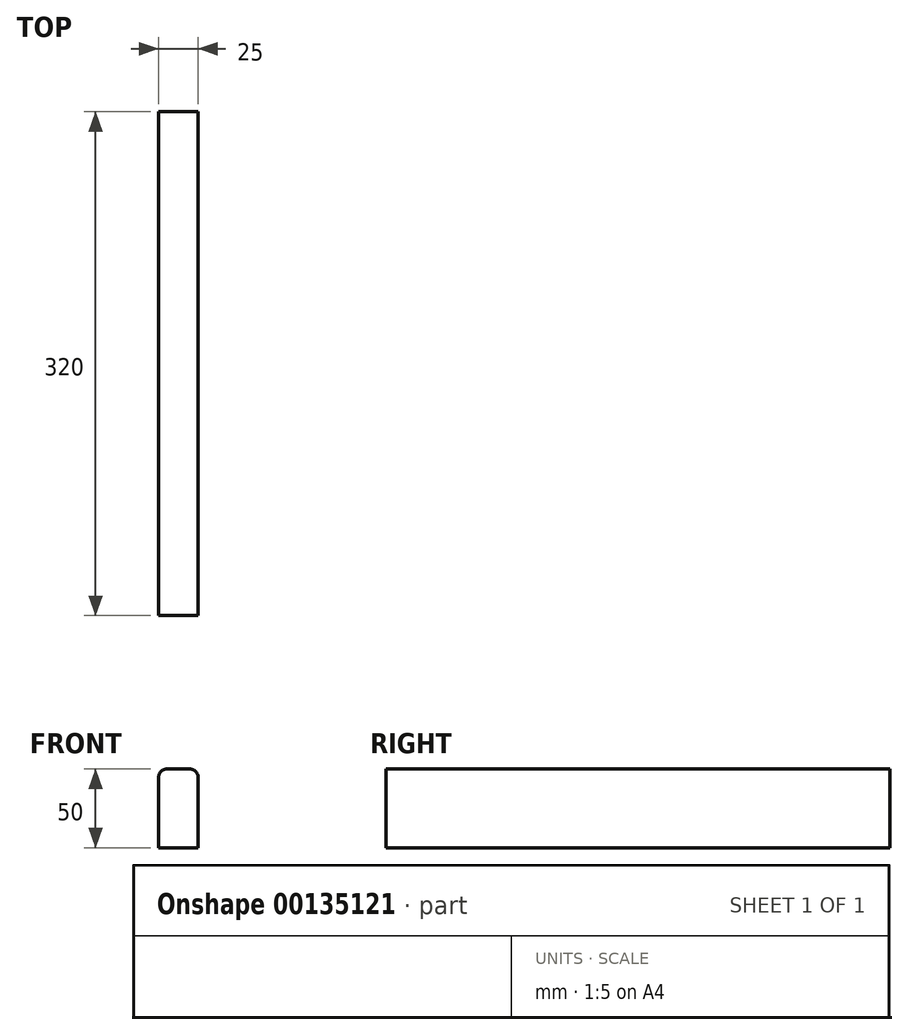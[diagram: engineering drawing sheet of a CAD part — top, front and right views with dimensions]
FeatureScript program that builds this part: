
annotation { "Feature Type Name" : "Feature", "Feature Type Description" : "" }
export const myFeature = defineFeature(function(context is Context, id is Id, definition is map)
    precondition{}
    {
        {
            var Q0;
            Q0=qCreatedBy(makeId("Front.planeOp"),FACE);
            var sketch = newSketch(context, id + "F0", { "sketchPlane" : qUnion([Q0])});
            skLineSegment(sketch, "E0.bottom", {"start": v(0, 0) * mm, "end": v(25, 0) * mm});
            skLineSegment(sketch, "E0.top", {"start": v(5, 50) * mm, "end": v(20, 50) * mm});
            skLineSegment(sketch, "E0.left", {"start": v(0, 0) * mm, "end": v(0, 45) * mm});
            skLineSegment(sketch, "E0.right", {"start": v(25, 0) * mm, "end": v(25, 45) * mm});
            skPoint(sketch, "E1.visualSharp", {"position": v(0, 50) * mm});
            skArc(sketch, "E1.filletArc", {"start": v(5, 50) * mm, "mid": v(1.46, 48.54) * mm, "end": v(0, 45) * mm});
            skPoint(sketch, "E2.visualSharp", {"position": v(25, 50) * mm});
            skArc(sketch, "E2.filletArc", {"start": v(25, 45) * mm, "mid": v(23.54, 48.54) * mm, "end": v(20, 50) * mm});
            skSolve(sketch);
        }
        {
            var Q0;
            Q0 = qSketchRegion(id + "F0", true);
            extrude(context, id + "F1", {"entities" : qUnion([Q0]), "depth" : 320 * mm});
        }
    });
